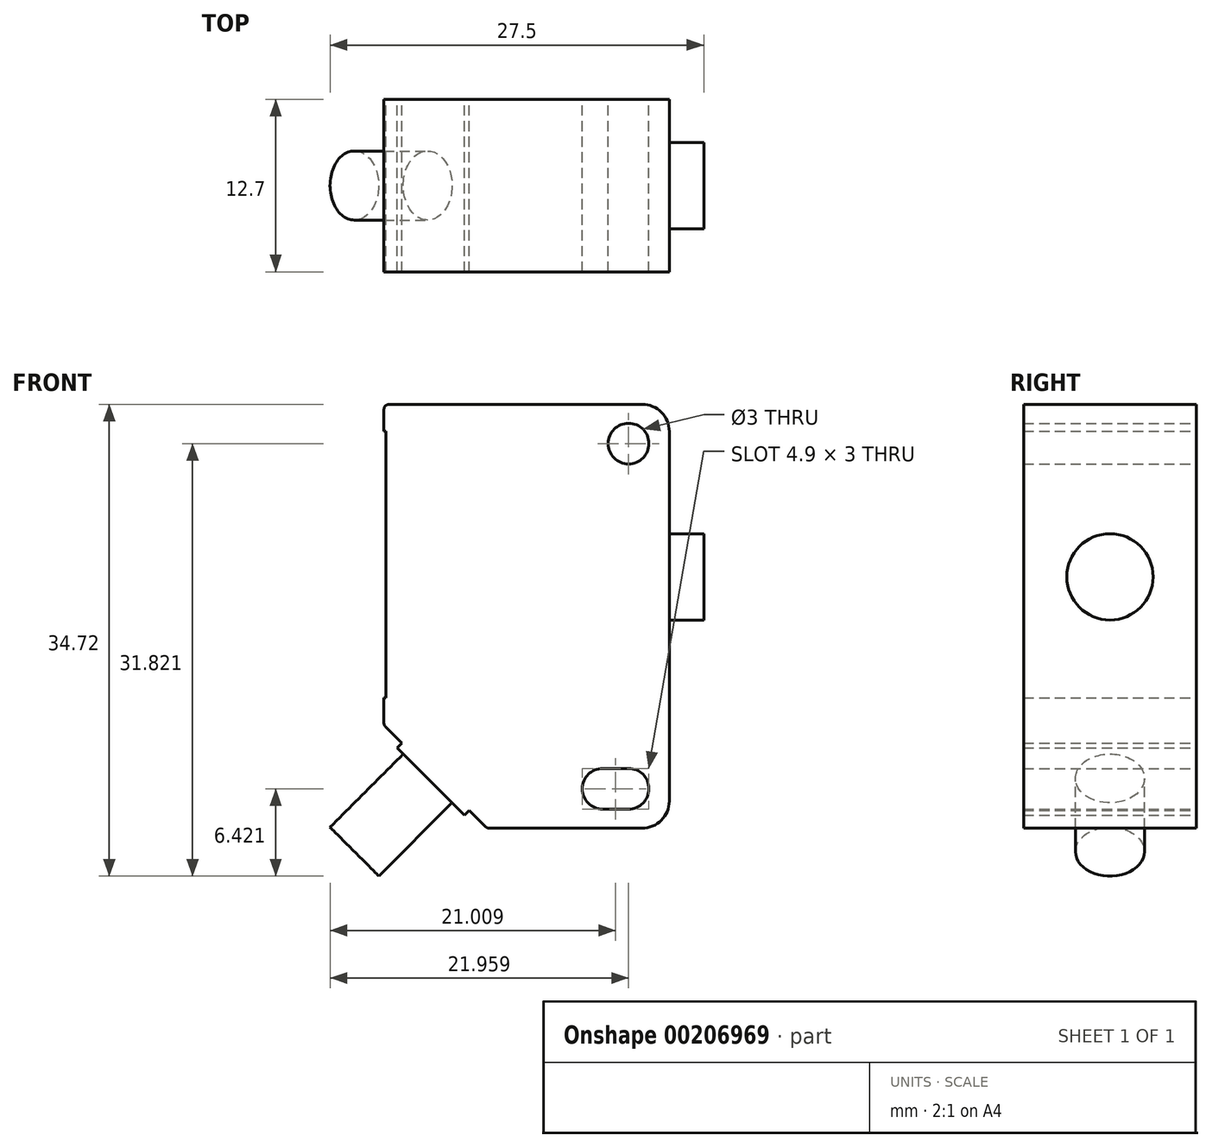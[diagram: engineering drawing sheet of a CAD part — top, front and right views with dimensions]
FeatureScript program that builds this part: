
annotation { "Feature Type Name" : "Feature", "Feature Type Description" : "" }
export const myFeature = defineFeature(function(context is Context, id is Id, definition is map)
    precondition{}
    {
        {
            var Q0;
            Q0=qCreatedBy(makeId("Front.planeOp"),FACE);
            var sketch = newSketch(context, id + "F0", { "sketchPlane" : qUnion([Q0])});
            skLineSegment(sketch, "E0", {"start": v(-64.71, 159.23) * mm, "end": v(-46.11, 159.23) * mm});
            skArc(sketch, "E1", {"start": v(-64.71, 159.23) * mm, "mid": v(-65, 159.11) * mm, "end": v(-65.11, 158.83) * mm});
            skLineSegment(sketch, "E2", {"start": v(-65.11, 157.23) * mm, "end": v(-65.11, 158.83) * mm});
            skLineSegment(sketch, "E3", {"start": v(-64.96, 157.23) * mm, "end": v(-65.11, 157.23) * mm});
            skLineSegment(sketch, "E4", {"start": v(-64.96, 137.63) * mm, "end": v(-64.96, 157.23) * mm});
            skLineSegment(sketch, "E5", {"start": v(-57.64, 128.15) * mm, "end": v(-58.84, 129.36) * mm});
            skArc(sketch, "E6", {"start": v(-57.64, 128.15) * mm, "mid": v(-57.5, 128.06) * mm, "end": v(-57.35, 128.03) * mm});
            skLineSegment(sketch, "E7", {"start": v(-65.11, 137.63) * mm, "end": v(-64.96, 137.63) * mm});
            skLineSegment(sketch, "E8", {"start": v(-65.11, 135.8) * mm, "end": v(-65.11, 137.63) * mm});
            skLineSegment(sketch, "E9", {"start": v(-63.8, 134.3) * mm, "end": v(-65, 135.5) * mm});
            skArc(sketch, "E10", {"start": v(-65.11, 135.8) * mm, "mid": v(-65.08, 135.64) * mm, "end": v(-65, 135.5) * mm});
            skLineSegment(sketch, "E11", {"start": v(-46.11, 128.03) * mm, "end": v(-57.35, 128.03) * mm});
            skCircle(sketch, "E12", {"center": v(-47.11, 156.33) * mm, "radius": 1.5 * mm});
            skArc(sketch, "E13", {"start": v(-49.01, 132.43) * mm, "mid": v(-50.51, 130.93) * mm, "end": v(-49.01, 129.43) * mm});
            skLineSegment(sketch, "E14", {"start": v(-47.11, 132.43) * mm, "end": v(-49.01, 132.43) * mm});
            skLineSegment(sketch, "E15", {"start": v(-49.01, 129.43) * mm, "end": v(-47.11, 129.43) * mm});
            skArc(sketch, "E16", {"start": v(-47.11, 129.43) * mm, "mid": v(-45.61, 130.93) * mm, "end": v(-47.11, 132.43) * mm});
            skArc(sketch, "E17", {"start": v(-46.11, 128.03) * mm, "mid": v(-44.7, 128.62) * mm, "end": v(-44.11, 130.03) * mm});
            skArc(sketch, "E18", {"start": v(-44.11, 157.23) * mm, "mid": v(-44.7, 158.65) * mm, "end": v(-46.11, 159.23) * mm});
            skLineSegment(sketch, "E19", {"start": v(-63.18, 126.62) * mm, "end": v(-66.52, 129.96) * mm});
            skLineSegment(sketch, "E20", {"start": v(-63.67, 133.48) * mm, "end": v(-66.53, 130.38) * mm});
            skLineSegment(sketch, "E21", {"start": v(-62.77, 126.62) * mm, "end": v(-59.67, 129.48) * mm});
            skArc(sketch, "E22", {"start": v(-63.18, 126.62) * mm, "mid": v(-62.98, 126.54) * mm, "end": v(-62.77, 126.62) * mm});
            skArc(sketch, "E23", {"start": v(-66.53, 130.38) * mm, "mid": v(-66.61, 130.17) * mm, "end": v(-66.52, 129.96) * mm});
            skLineSegment(sketch, "E24", {"start": v(-44.11, 157.23) * mm, "end": v(-44.11, 130.03) * mm});
            skLineSegment(sketch, "E25", {"start": v(-44.1, 153.13) * mm, "end": v(-44.11, 153.13) * mm});
            skLineSegment(sketch, "E26", {"start": v(-44.11, 134.11) * mm, "end": v(-44.1, 134.11) * mm});
            skLineSegment(sketch, "E27", {"start": v(-64.15, 133.95) * mm, "end": v(-63.8, 134.3) * mm});
            skLineSegment(sketch, "E28", {"start": v(-59.2, 129) * mm, "end": v(-64.15, 133.95) * mm});
            skLineSegment(sketch, "E29", {"start": v(-63.82, 126.68) * mm, "end": v(-63.53, 126.97) * mm});
            skLineSegment(sketch, "E30", {"start": v(-66.18, 129.62) * mm, "end": v(-66.47, 129.33) * mm});
            skArc(sketch, "E31", {"start": v(-68.68, 128.41) * mm, "mid": v(-67.48, 128.65) * mm, "end": v(-66.47, 129.33) * mm});
            skArc(sketch, "E32", {"start": v(-68.68, 124.66) * mm, "mid": v(-66.05, 125.19) * mm, "end": v(-63.82, 126.68) * mm});
            skLineSegment(sketch, "E33", {"start": v(-47.11, 128.6) * mm, "end": v(-47.11, 158.65) * mm});
            skLineSegment(sketch, "E34", {"start": v(-50.51, 156.33) * mm, "end": v(-43.71, 156.33) * mm});
            skLineSegment(sketch, "E35", {"start": v(-51.31, 130.93) * mm, "end": v(-44.63, 130.93) * mm});
            skLineSegment(sketch, "E36", {"start": v(-49.01, 133.26) * mm, "end": v(-49.01, 128.6) * mm});
            skLineSegment(sketch, "E37", {"start": v(-59.2, 129) * mm, "end": v(-58.84, 129.36) * mm});
            skSolve(sketch);
        }
        {
            var Q0;
            Q0=makeQuery(id+"F0.imprint","IMPRINT",FACE,{"disambiguationData":[TD([[makeQuery(id+"F0.imprint","IMPRINT",EDGE,{"derivedFrom":sQuery(id+"F0.wireOp",EDGE,"E0")}),-1.0]])]});
            extrude(context, id + "F1", {"entities" : qUnion([Q0]), "depth" : 12.7 * mm});
        }
        {
            var Q0;
            Q0=makeQuery(id+"F1.opExtrude","SWEPT_FACE",FACE,{"disambiguationData":[OSD([sQuery(id+"F0.wireOp",EDGE,"E28")])]});
            var sketch = newSketch(context, id + "F2", { "sketchPlane" : qUnion([Q0])});
            skCircle(sketch, "E38", {"center": v(6.35, 136.89) * mm, "radius": 2.54 * mm});
            skSolve(sketch);
        }
        {
            var Q0;
            Q0=qSketchRegion(id+"F2",true);
            extrude(context, id + "F3", {"entities" : qUnion([Q0]), "operationType" : NewBodyOperationType.ADD, "depth" : 7.62 * mm});
        }
        {
            var Q0;
            Q0=makeQuery(id+"F1.opExtrude","SWEPT_FACE",FACE,{"disambiguationData":[OSD([sQuery(id+"F0.wireOp",EDGE,"E24")])]});
            var sketch = newSketch(context, id + "F4", { "sketchPlane" : qUnion([Q0])});
            skCircle(sketch, "E39", {"center": v(-6.35, 146.53) * mm, "radius": 3.18 * mm});
            skSolve(sketch);
        }
        {
            var Q0;
            Q0=qSketchRegion(id+"F4",true);
            extrude(context, id + "F5", {"entities" : qUnion([Q0]), "operationType" : NewBodyOperationType.ADD, "depth" : 2.54 * mm});
        }
    });
